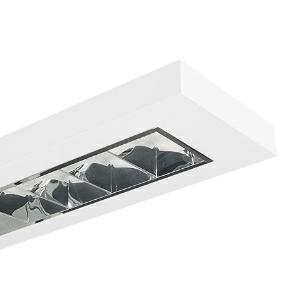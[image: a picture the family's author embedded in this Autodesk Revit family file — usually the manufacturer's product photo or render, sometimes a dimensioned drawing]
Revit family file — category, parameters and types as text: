
# Revit family: 3f_filippi_-_3f_travetta_di_2mg_3f_filippi_-_11503_-_3f_travetta_led_di_2x15w_dali_2mg_l1590
name_source: partatom
category: Lighting Fixtures
units: mm (PartAtom-declared; Revit-internal decimal feet)

## family parameters
Cut with Voids When Loaded = No
Host = Face
Light Source = No
Part Type = Normal
Room Calculation Point = No
Round Connector Dimension = Use Diameter
Shared = No

## types (1)
- 3F Filippi - 3F Travetta DI 2MG (1 x LED, 3958 lm, 33 W, 4000 K)
    Apparent Load = 33 VA
    Approval mark = ENEC
    CIE Flux Codes = 61 98 100 85 100
    Color Rendering = 80
    Color Temperature = 4000 K
    Control Gear = Electronic transformer
    Default Elevation = 1800 mm
    Description = ILLUMINOTECHNICAL
Luminous efficiency 100% (DLOR 85%, ULOR 15%).
Initial luminous flux of the luminaire 3958 lm.
Symmetric direct-indirect distribution.
Installation Interdistance Transv.D = 2.02 x hu - Long.D = 1.27 x hu.
Average luminance <1000 cd/m² for radial angles >65°.
Tabular UGR (CIE 117 - 4H-8H; S=0.25H; 70/50/20): RUG 17.1 - 16.4.
Beam angle: 99° - 72°.
Luminous efficacy 120 lm/W.
Lifetime (L93/B10): 30000 h. (tq+25°C)
Lifetime (L90/B10): 50000 h. (tq+25°C)
Lifetime (L85/B10): 80000 h. (tq+25°C)
Lifetime (L80/B10): 100000 h. (tq+25°C)
Sudden decreased luminous flux after 50000 hours: 0% (C0).
Photobiological safety in compliance with IEC/TR 62778: RG0 risk exempt, (IEC 62471).
In compliance with IEC/EN 62722-2-1 - IEC/EN 62717 standards.

SOURCE
2 linear LED modules 15W/840.
Energy efficiency class (UE 2019/2020 - UE 2019/2015): D.
CIE 13.3 Colour rendering index: CRI >80 (R9 <50%).
IES TM-30 Fidelity Index: Rf = 84 Rg = 95.
CCT nominal colour temperature 4000 K.
Colour initial tolerance (MacAdam): SDCM 2.

MECHANICAL
Housing with squared shape in white painted galvannealed steel, with nonreflecting surface.
2MG parabolic louvre, high efficiency, in specular aluminium with superficial titanium-magnesium treatment, non-iridescent, with transverse blades closed at the top.
Prismatic flat diffuser in transparent methacrylate (PMMA), multilenticular, anti-glare, prismatic exterior, placed above louvre blades.
Film protective against dust and finger marks, adhesive, attached to louvre.
Upper holes closing film made of opal polycarbonate.
Luminaire with limited surface temperature. - D - (EN 60598-2-24)
Dimensions: 1590x190 mm, height 60 mm (edge 40 mm). Weight 5.045 kg.
IP20 protection degree.
Mechanical strength to impacts IK02 (0.2 joule).
Glow-wire test resistance 650°C.

ELECTRICAL
Halogen Free DALI-2 DATI (Parts 251, 252, 253), PUSH-DIM, electronic wiring 230V-50/60Hz, power factor 0.95 at full load, THD <25%, constant output current, SELV, class I, 1 driver, 1 DALI addresse.
Power of the luminaire 33 W.
CE - IEC 60598-1 - EN 60598-1.
SAFE FLICKER: PstLM=<1 and SVM=<0.4 (IEC TR 61547-1 and IEC TR 63158), to ensure a more comfortable and safe light.
Luminaire compliant with EN 60598-2-22 for power supply from a centralised emergency system CPSS (Central Power Supply System), not incorporated in the luminaire - high risk areas excluded. The default power and flux are 100% in AC and 15% in DC.
Ambient temperature from 0°C to +25°C.
Temperature class T6 max 85°C.
Relative humidity UR: <85%.

INSTALLATION
Suspended.
All accessories dedicated to this product are available on the Catalog and on our website www.3F-Filippi.com.

APPLICATIONS
In environments, even with reduced height, requiring a comfortable light.
In environments with VDTs, managerial offices and staterooms, public offices and schools.

LIGHT MANAGEMENT
Recommended minimum setting: 10%.
The luminaire, equipped with (DALI-2 DATI) driver, can be controlled manually with 3F Easy Dim technology or automatically/manually with wired or wireless DALI/D2D control systems.
The D2D driver guarantees interoperability with other devices with the same certification by making the following information available:
Device Data (Part 251), Energy Report (Part 252), Diagnosis & Maintenance (Part 253).
In electrical systems without a regulation system (manual or automatic) and DALI bus, a suitable jumper must be made on the DA-DA terminals of the appliance.

WARNING
Luminaire designed for disposal/recycling at end-of-life.
Replaceable (LED only) light source by a professional. Replaceable control gear by a professional.
    Height = 60 mm  [stored 0.19685 ft]
    Lamp = 1 x LED
    Lamp Light Flux = 3958 lm
    Lamp Power = 33 W
    Lamp count = 1
    Length = 1590 mm
    Lifetime = 50000 h
    Luminous efficacy = 120 lm/W
    Manufacturer = 3F Filippi
    ModVariant = No
    Model = 3F Filippi - 11503 - 3F Travetta LED DI 2x15W DALI 2MG L1590
    Mounting Place = Ceiling
    Mounting Type = Pendant
    Number of Poles = 1
    OnlyDefault = Yes
    Power Factor = 1
    Product Name = 3F Filippi - 3F Travetta DI 2MG
    Product group = pendant luminaire
    ProductGroupID = 9
    Protection Class = Protection class I
    Protection Degree = IP 20
    RLX_Detail_Level = 1
    RLX_Emergency_Light_Flux = 0 lm
    RLX_Emergency_Type = 0
    RLX_Emergency_Type_DB = No
    RlxData = <blob elided: 53737 chars, md5=932d284c>
    Socket = socket
    Standby Power = 0 W
    System Light Flux = 3958 lm
    System Power = 33 W
    Type Comments = Product without accessories
    Type Image = 3ffilippi_3f_travetta_led_2mg.jpg
    URL = http://relux.com
    VarID = ---
    Voltage = 0 V
    Weight = 0.00 kg
    Width = 190 mm  [stored 0.62336 ft]

note: [stored X ft] marks values corroborated as IEEE doubles in the binary element streams (Revit-internal decimal feet)

## geometry (parser evidence)
native form markers: Blend x4, Sweep x13
no freeform markers — native parametric forms only
